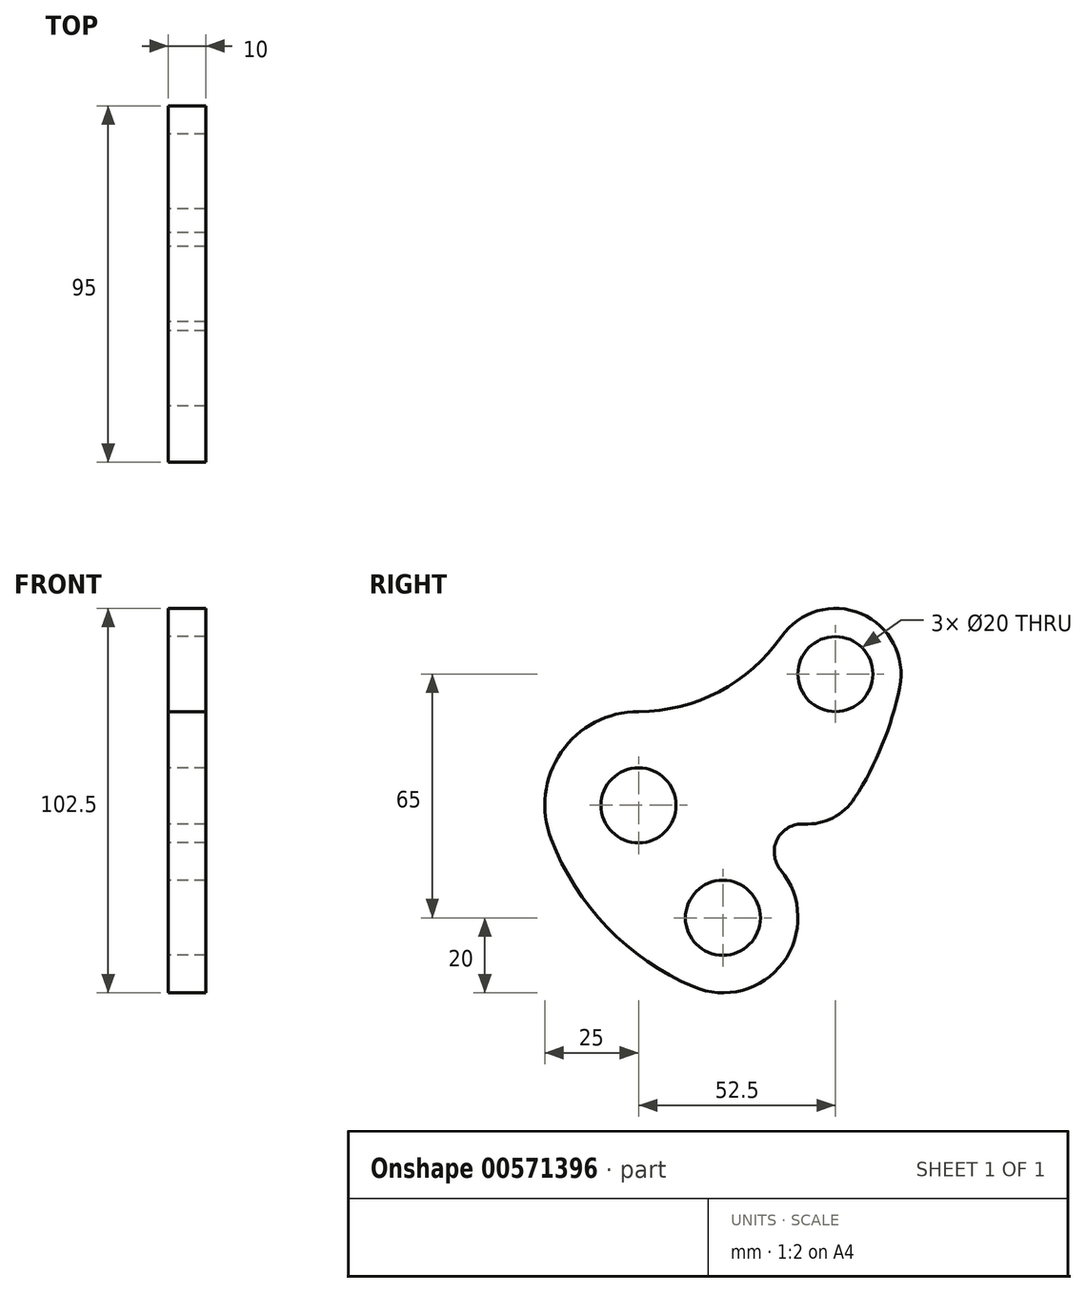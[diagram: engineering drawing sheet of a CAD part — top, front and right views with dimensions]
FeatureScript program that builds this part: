
annotation { "Feature Type Name" : "Feature", "Feature Type Description" : "" }
export const myFeature = defineFeature(function(context is Context, id is Id, definition is map)
    precondition{}
    {
        {
            var Q0;
            Q0=qCreatedBy(makeId("Right.planeOp"),FACE);
            var sketch = newSketch(context, id + "F0", { "sketchPlane" : qUnion([Q0])});
            skCircle(sketch, "E0", {"center": v(0, 0) * mm, "radius": 10 * mm});
            skCircle(sketch, "E1", {"center": v(52.5, 35) * mm, "radius": 10 * mm});
            skCircle(sketch, "E2", {"center": v(22.5, -30) * mm, "radius": 10 * mm});
            skArc(sketch, "E3", {"start": v(0, 25) * mm, "mid": v(-20.6, 14.16) * mm, "end": v(-23.34, -8.96) * mm});
            skArc(sketch, "E4", {"start": v(14.64, -48.39) * mm, "mid": v(38.52, -41.97) * mm, "end": v(37.9, -17.24) * mm});
            skArc(sketch, "E5", {"start": v(69.64, 31.48) * mm, "mid": v(59.38, 51.1) * mm, "end": v(38.11, 44.96) * mm});
            skArc(sketch, "E6", {"start": v(-23.36, -8.9) * mm, "mid": v(-8.37, -32.5) * mm, "end": v(14.64, -48.39) * mm});
            skLineSegment(sketch, "E7", {"start": v(0, 0) * mm, "end": v(0, 59.8) * mm, "construction": true});
            skArc(sketch, "E8", {"start": v(0, 25) * mm, "mid": v(21.51, 30.3) * mm, "end": v(38.11, 44.96) * mm});
            skArc(sketch, "E9", {"start": v(44.12, -4.97) * mm, "mid": v(51.81, -3.36) * mm, "end": v(57.63, 1.91) * mm});
            skArc(sketch, "E10", {"start": v(69.64, 31.48) * mm, "mid": v(64.69, 15.4) * mm, "end": v(56.74, 0.54) * mm});
            skLineSegment(sketch, "E11", {"start": v(45, 10) * mm, "end": v(45, -41.77) * mm, "construction": true});
            skArc(sketch, "E12", {"start": v(45, -5.08) * mm, "mid": v(37.2, -8.68) * mm, "end": v(37.9, -17.24) * mm});
            skSolve(sketch);
        }
        {
            var Q0;
            Q0=makeQuery(id+"F0.imprint","IMPRINT",FACE,{"disambiguationData":[TD([[makeQuery(id+"F0.imprint","IMPRINT",EDGE,{"derivedFrom":sQuery(id+"F0.wireOp",EDGE,"E0")}),-1.0]])]});
            extrude(context, id + "F1", {"entities" : qUnion([Q0]), "depth" : 10 * mm, "offsetDistance" : 25 * mm});
        }
    });
